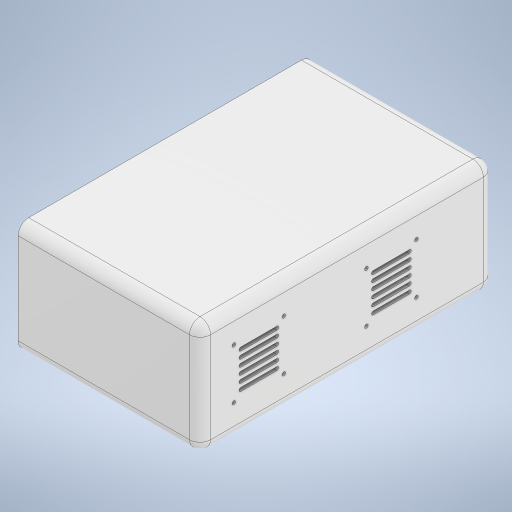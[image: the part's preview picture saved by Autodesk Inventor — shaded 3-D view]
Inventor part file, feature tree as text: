
AUTODESK INVENTOR PART (.ipt)
format: ipt  version: 2023 (Build 270158000, 158)  size: 1,345,536 bytes
history: native  units: in
note: dims shown in document units (in); Inventor stores cm internally (conversion verified against a paired STEP export)
features: sketch x15, extrude x11, fillet x11, chamfer x10, pattern_linear x5, hole x4, plane x3, shell x1, mirror x1
ambient origin geometry x8: Origin, YZ Plane, XZ Plane, XY Plane, X Axis, Y Axis, Z Axis, Center Point
bodies: Solid1 (feature_tree)
feature tree (61):
  extrude  "Extrusion1"  Depth=10.2362in
  shell  "Shell1"  Thickness=6.2992in
  extrude  "Extrusion4"  Depth=0.1969in
  extrude  "Extrusion5"  Depth=0.9055in
  extrude  "Extrusion6"  Depth=0.3937in
  hole  "Hole1"  [1 undecoded]
  fillet  "Fillet14"  Radius=0.5906in
  extrude  "Extrusion7"  Depth=0.7874in
  fillet  "Fillet18"  Radius=0.7874in
  fillet  "Fillet19"  Radius=0.7874in
  fillet  "Fillet20"  Radius=0.0787in
  chamfer  "Chamfer1"  Distance=0.0787in
  chamfer  "Chamfer2"  Distance=0.0787in
  chamfer  "Chamfer3"  Distance=0.0787in
  chamfer  "Chamfer4"  Distance=0.0787in
  chamfer  "Chamfer5"  Distance=0.0787in
  plane  "Work Plane1"
  hole  "Hole2"  [1 undecoded]
  hole  "Hole3"  [1 undecoded]
  hole  "Hole4"  [1 undecoded]
  extrude  "Extrusion11"  Depth=0.1575in
  fillet  "Fillet21"  Radius=0.5906in
  pattern_linear  "Rectangular Pattern3"  Spacing1=0.3937in  [1 undecoded]
  extrude  "Extrusion12"  Depth=0.1969in
  fillet  "Fillet23"  Radius=0.1575in
  pattern_linear  "Rectangular Pattern4"  Spacing1=0.0197in  [1 undecoded]
  plane  "Work Plane4"
  plane  "Work Plane5"
  extrude  "Extrusion15"  Depth=0.1575in TaperAngle=60.0deg
  pattern_linear  "Rectangular Pattern6"  Spacing1=0.0394in  [1 undecoded]
  extrude  "Extrusion16"  Depth=0.1575in TaperAngle=60.0deg
  fillet  "Fillet25"  Radius=0.0394in
  fillet  "Fillet27"  Radius=2.815in
  fillet  "Fillet28"  Radius=2.815in
  fillet  "Fillet29"  Radius=5.5118in
  extrude  "Extrusion17"  Depth=0.1575in
  fillet  "Fillet30"  Radius=2.815in
  sketch  "Sketch28"  dims[d66=0.0787in]
  extrude  "Extrusion24"  Depth=0.1575in
  mirror  "Mirror8"
  pattern_linear  "Rectangular Pattern9"  Spacing1=2.815in  [1 undecoded]
  pattern_linear  "Rectangular Pattern10"  Count1=2  [1 undecoded]
  chamfer  "Chamfer10"  Distance=0.7874in
  chamfer  "Chamfer11"  Distance=2.815in
  chamfer  "Chamfer12"  Distance=2.815in
  chamfer  "Chamfer13"  Distance=3.1496in
  chamfer  "Chamfer14"  Distance=3.1496in
  sketch  "Sketch1"  dims[d0=16.5354in d1=10.2362in d2=6.2992in d3=0.0in]
  sketch  "Sketch4"  dims[d4=0.1969in d17=0.1969in]
  sketch  "Sketch5"  dims[d20=3.937in d21=0.0in d22=0.9055in]
  sketch  "Sketch6"  dims[d23=0.3937in d24=0.0in d28=0.3937in]
  sketch  "Sketch9"  dims[d29=0.3937in d30=0.3937in d31=0.0in]
  sketch  "Sketch10"  dims[d40=0.4016in d41=0.2362in d42=0.1575in d43=0.0787in d44=90.0deg d45=9.4488in d46=0.0in d50=0.5906in]
  sketch  "Sketch14"  dims[d54=0.7874in d55=0.7874in d56=0.7874in d57=0.7874in d58=0.0787in]
  sketch  "Sketch15"  dims[d59=0.0787in]
  sketch  "Sketch17"  dims[d61=0.0787in]
  sketch  "Sketch18"  dims[d62=0.0787in]
  sketch  "Sketch21"  dims[d63=0.0787in]
  sketch  "Sketch23"  dims[d64=0.0787in]
  sketch  "Sketch24"  dims[d65=0.0787in]
  sketch  "Sketch29"  dims[d67=0.0787in d68=0.0787in d69=0.0787in d70=0.0787in d72=0.0787in d73=0.0787in d74=0.0787in d75=0.0in d76=0.5906in d77=0.5906in d78=0.5906in d79=0.5906in d80=0.3937in d81=0.1969in d82=0.1575in d83=0.0197in d84=0.0787in d85=45.0deg d86=0.0394in d87=0.0787in d88=60.0deg d89=0.0394in d90=0.0787in d91=60.0deg d92=0.0394in d93=0.0787in d94=60.0deg d95=0.0394in d96=0.0787in d97=60.0deg d137=2.815in d138=2.815in d139=0.1969in d140=0.2362in d141=0.1575in d142=0.0787in d143=90.0deg d144=0.315in d145=0.8108in d146=5.5118in d147=2.815in d148=2.815in d149=0.1969in d150=0.2362in d151=0.1575in d152=0.0787in d153=90.0deg d154=0.315in d155=0.8108in d156=2.815in d157=2.815in d159=0.7874in d160=0.1969in d161=0.2362in d162=0.1575in d163=0.0787in d164=90.0deg d165=0.315in d166=0.8108in d167=0.7874in d168=2.815in d169=2.815in d170=3.1496in d171=3.1496in d172=0.1969in d173=0.1969in d174=0.0in d175=0.0in d176=2.3622in d178=0.3937in d179=3.1496in d180=3.1496in d181=0.1969in d182=0.1969in d183=0.1969in d184=0.0in d185=2.3622in d187=0.3937in d192=0.0984in d194=0.0984in d209=1.5748in d210=1.5748in d211=1.378in d212=0.9843in d213=0.0787in d214=0.0in d215=0.7874in d217=6.1024in d245=0.0787in d246=0.6299in d247=2.3622in d248=3.1496in d249=0.3937in d250=0.0in d251=0.315in d256=0.315in d257=0.2362in d258=0.5906in d260=0.5906in d261=0.1969in d262=0.3937in d263=0.0in d264=0.0787in d295=0.1575in d296=0.0787in d297=0.0787in d298=0.315in d299=0.3937in d300=7.874in d301=0.0in d302=1.1811in d304=1.7717in d305=0.5512in d306=1.1811in d308=1.7717in d309=0.3937in d310=0.0787in d311=30.0deg d312=0.3937in d313=0.0787in d314=30.0deg d315=0.3937in d316=0.0787in d317=30.0deg d318=0.3543in d319=0.1575in d320=30.0deg d321=0.3543in d322=0.1575in d323=30.0deg d324=0.0787in d325=0.0787in]
note: 9 required parameter values undecoded (feature->parameter linkage not recoverable at this tier; creation-order binding heuristic only, values carry confidence <= 0.55)
